# Revit family: Domotics-NetworkCabling-GEWISS-CABINETS_WALL-MOUNTED_19_6U_D400
name_source: partatom
category: Apparecchi elettrici
units: mm (PartAtom-declared; Revit-internal decimal feet)

## family parameters
Condiviso = No
Host = Superficie
Mantenere orientamento annotazione = Sì
Punto di calcolo locali = Sì
Quota connettore circolare = Usa diametro
Taglio con vuoti quando caricato = No
Tipo di parte = Normale

## types (1)
- GW38406 - WALL CABINET 19 U DEPTH 400MM.
    Cabling unity = 6 U
    Catalogue = DOMOTICS
    Category = 19â€ wall-mount cabinet
    Colour = Grey (RAL 7035)
    Depth (mm) = 400 mm
    Descrizione = WALL CABINET 19 U DEPTH 400MM.
    Door opening = 180°
    Electrocod = 3752
    Finishing = Textured
    IDF = 58b718b1-f27f-4b1c-94a8-e583979b338f
    IDT = 1607453e44e34c9e8499f282ce5acb34
    IP degree = IP20
    Immagine tipo = B.jpg
    L_quadro = 325 mm
    Material = Steel
    Modello = GW38406
    No. uprights = 2
    Outer dim. LxHxD (mm) = 600x335x400
    Produttore = GEWISS S.p.A.
    Prospetto di default = 1219 mm
    SEO = Board
    Static load capacity = 50KG
    Technical sheet = https://www.gewiss.com
    Type of door = Reversible
    URL = https://www.gewiss.com
    Version file RFA = 21.2
    a = 15.00°
    h_quadro = 400 mm  [stored 1.31234 ft]
    p_quadro = 263 mm

note: [stored X ft] marks values corroborated as IEEE doubles in the binary element streams (Revit-internal decimal feet)

## geometry (parser evidence)
native form markers: Sweep x4
no freeform markers — native parametric forms only
